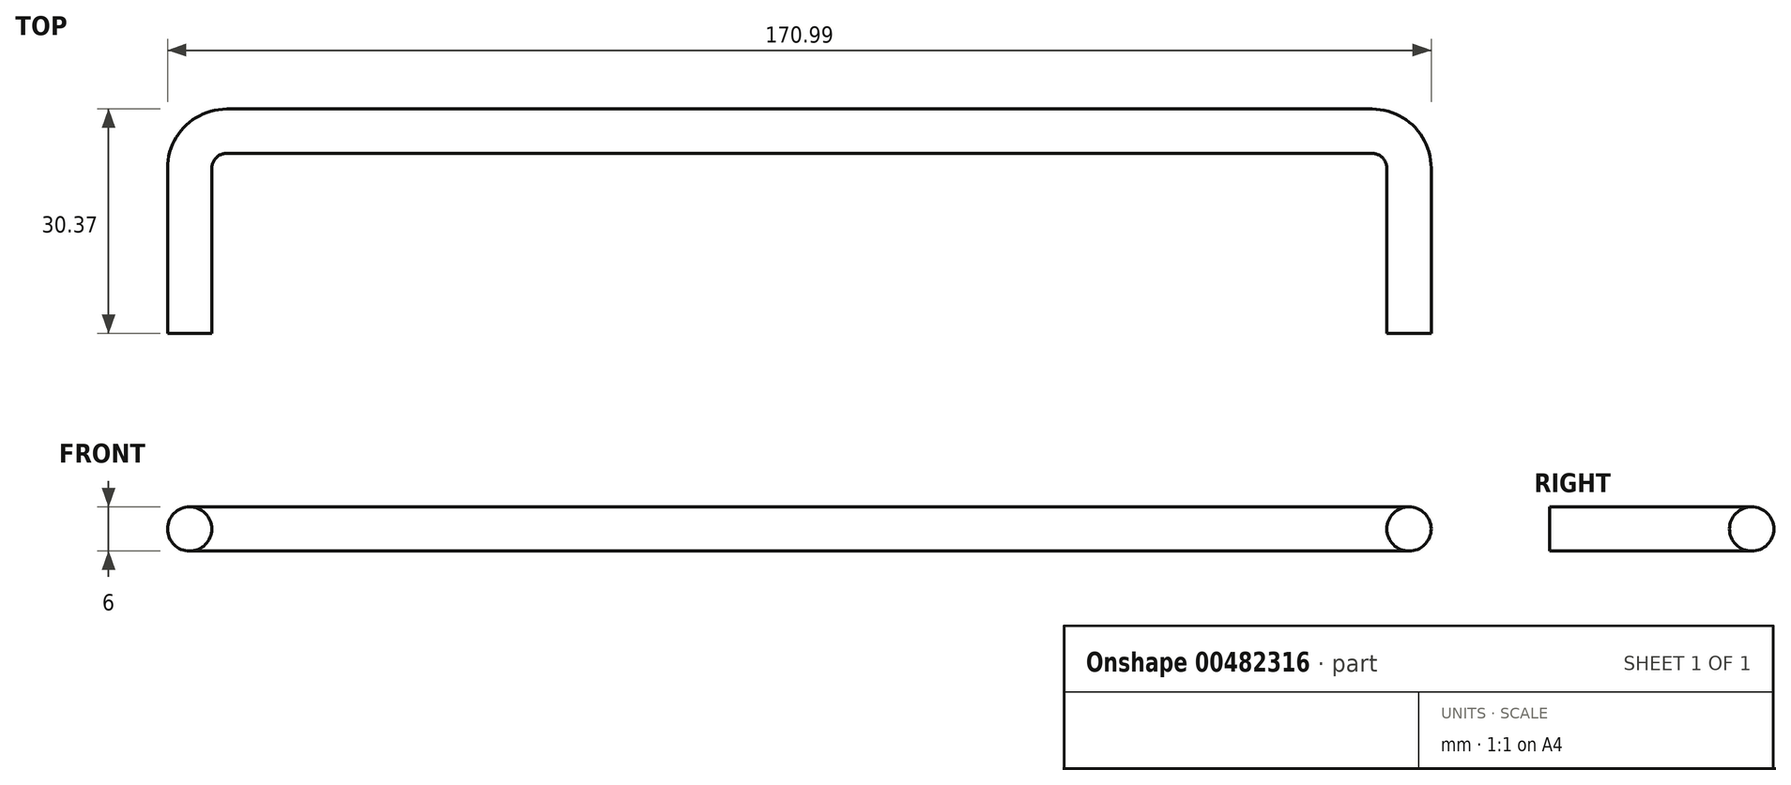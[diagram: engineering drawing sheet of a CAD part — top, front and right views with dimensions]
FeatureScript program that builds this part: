
annotation { "Feature Type Name" : "Feature", "Feature Type Description" : "" }
export const myFeature = defineFeature(function(context is Context, id is Id, definition is map)
    precondition{}
    {
        {
            var Q0;
            Q0=qCreatedBy(makeId("Top.planeOp"),FACE);
            var sketch = newSketch(context, id + "F0", { "sketchPlane" : qUnion([Q0])});
            skLineSegment(sketch, "E0", {"start": v(-46.44, 36.1) * mm, "end": v(108.56, 36.1) * mm});
            skLineSegment(sketch, "E1", {"start": v(113.56, 31.1) * mm, "end": v(113.56, 8.72) * mm});
            skLineSegment(sketch, "E2", {"start": v(-51.44, 31.1) * mm, "end": v(-51.44, 8.72) * mm});
            skPoint(sketch, "E3.visualSharp", {"position": v(-51.44, 36.1) * mm});
            skArc(sketch, "E3.filletArc", {"start": v(-46.44, 36.1) * mm, "mid": v(-49.97, 34.63) * mm, "end": v(-51.44, 31.1) * mm});
            skPoint(sketch, "E4.visualSharp", {"position": v(113.56, 36.1) * mm});
            skArc(sketch, "E4.filletArc", {"start": v(113.56, 31.1) * mm, "mid": v(112.1, 34.63) * mm, "end": v(108.56, 36.1) * mm});
            skLineSegment(sketch, "E5", {"start": v(113.56, 8.72) * mm, "end": v(104.8, 8.72) * mm});
            skSolve(sketch);
        }
        {
            var Q0;
            Q0=qCreatedBy(id+"FqiWXO5US18zetI.pointOp",VERTEX);
            var Q1;
            Q1=sQuery(id+"F0.wireOp",EDGE,"E5");
            cPlane(context, id + "F1", {"entities" : qUnion([Q0, Q1]), "cplaneType" : CPlaneType.LINE_ANGLE, "offset" : 25 * mm, "angle" : 0 * degree, "width" : 150 * mm, "height" : 150 * mm});
        }
        {
            var Q0;
            Q0=sQuery(id+"F0.wireOp",EDGE,"E5");
            cPlane(context, id + "F2", {"entities" : qUnion([Q0]), "cplaneType" : CPlaneType.LINE_ANGLE, "offset" : 25 * mm, "angle" : 0 * degree, "width" : 150 * mm, "height" : 150 * mm});
        }
        {
            var Q0;
            Q0=qCreatedBy(id+"F2.planeOp",FACE);
            var sketch = newSketch(context, id + "F3", { "sketchPlane" : qUnion([Q0])});
            skCircle(sketch, "E6", {"center": v(1115.96, 0) * mm, "radius": 0.1 * mm});
            skCircle(sketch, "E7", {"center": v(113.56, 0) * mm, "radius": 3 * mm});
            skSolve(sketch);
        }
        {
            var Q0;
            Q0=makeQuery(id+"F3.imprint","IMPRINT",FACE,{"disambiguationData":[TD([[makeQuery(id+"F3.imprint","IMPRINT",EDGE,{"derivedFrom":sQuery(id+"F3.wireOp",EDGE,"E7")}),1.0]])]});
            var Q1;
            Q1=sQuery(id+"F0.wireOp",EDGE,"E1");
            var Q2;
            Q2=sQuery(id+"F0.wireOp",EDGE,"E4.filletArc");
            var Q3;
            Q3=sQuery(id+"F0.wireOp",EDGE,"E0");
            var Q4;
            Q4=sQuery(id+"F0.wireOp",EDGE,"E3.filletArc");
            var Q5;
            Q5=sQuery(id+"F0.wireOp",EDGE,"E2");
            sweep(context, id + "F4", {"profiles" : qUnion([Q0]), "path" : qUnion([Q1, Q2, Q3, Q4, Q5])});
        }
    });
